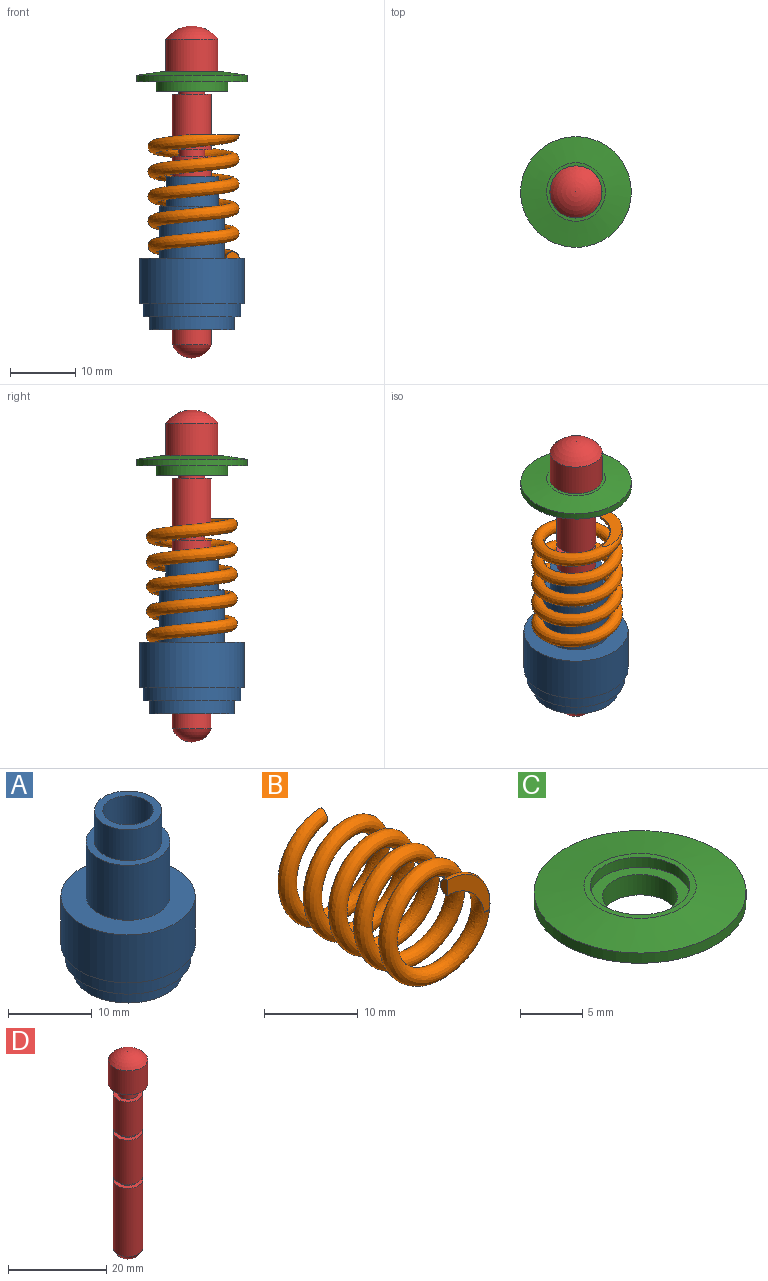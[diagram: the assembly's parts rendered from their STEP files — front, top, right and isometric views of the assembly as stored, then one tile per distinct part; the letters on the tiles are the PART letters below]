
ASSEMBLY  parts=4 mates=4
PART A: 12 faces, bbox 16x16x23.5 mm
  f0: plane 8x8mm, normal (0,0,1), area 22mm2, adj f1,f11
  f1: cylinder r=3mm len=23.5mm, axis (0,0,1), area 443mm2, adj f0,f2
  f2: plane 13x13mm, normal (0,0,-1), area 104.5mm2, adj f1,f3
  f3: cylinder r=6.5mm len=13mm, axis (0,0,1), area 81.7mm2, adj f2,f4
  f4: plane 15x15mm, normal (0,0,-1), area 44mm2, adj f3,f5
  f5: cylinder r=7.5mm len=15mm, axis (0,0,1), area 94.2mm2, adj f4,f6
  f6: plane 16x16mm, normal (0,0,-1), area 24.3mm2, adj f5,f7
  f7: cylinder r=8mm len=16mm, axis (0,0,1), area 351.9mm2, adj f6,f8
  f8: plane 16x16mm, normal (0,0,1), area 122.5mm2, adj f7,f9
  f9: cylinder r=5mm len=10mm, axis (0,0,1), area 251.3mm2, adj f8,f10
  f10: plane 10x10mm, normal (0,0,1), area 28.3mm2, adj f9,f11
  f11: cylinder r=4mm len=8mm, axis (0,0,1), area 113.1mm2, adj f0,f10
PART B: 6 faces, bbox 14.5x21.5x14.5 mm
  f0: bspline ~21x13.99mm, area 1149.5mm2, adj f1,f2,f3,f4,f5
  f1: plane 2.28x1.28mm, normal (1,0,0), area 1.6mm2, adj f0,f3
  f2: plane 2.28x1.28mm, normal (-1,0,0), area 1.6mm2, adj f0,f5
  f3: plane 7.47x6.45mm, normal (0,1,0), area 15.6mm2, adj f0,f1
  f4: plane 0.64x0.07mm, normal (0,0,1), area 0mm2, adj f0,f5
  f5: plane 7.5x6.95mm, normal (0,-1,0), area 15.4mm2, adj f0,f2,f4
PART C: 9 faces, bbox 17x17x3 mm
  f0: cylinder r=3mm len=6mm, axis (0,0,1), area 37.7mm2, adj f1,f8
  f1: plane 11x11mm, normal (0,0,-1), area 66.8mm2, adj f0,f2
  f2: cylinder r=5.5mm len=11mm, axis (0,0,1), area 49mm2, adj f1,f3
  f3: plane 17x17mm, normal (0,0,-1), area 131.9mm2, adj f2,f4
  f4: cylinder r=8.5mm len=17mm, axis (0,0,1), area 53.4mm2, adj f3,f5
  f5: cone r=8.5mm half-angle=81.7deg, axis (0,0,-1), area 165.1mm2, adj f4,f6
  f6: plane 9x9mm, normal (0,0,1), area 13.4mm2, adj f5,f7
  f7: cylinder r=4mm len=8mm, axis (0,0,1), area 25.1mm2, adj f6,f8
  f8: plane 8x8mm, normal (0,0,1), area 22mm2, adj f0,f7
PART D: 15 faces, bbox 8x8x51 mm
  f0: plane 8x8mm, normal (0,0,-1), area 37.7mm2, adj f1,f14
  f1: cylinder r=4mm len=8mm, axis (0,0,-1), area 150.8mm2, adj f0,f2
  f2: sphere r=5mm, area 62.8mm2, adj f1
  f3: sphere r=3.25mm, area 40.8mm2, adj f4
  f4: cylinder r=3mm len=17mm, axis (0,0,-1), area 320.4mm2, adj f3,f5
  f5: plane 6x6mm, normal (0,0,1), area 15.7mm2, adj f4,f6
  f6: cylinder r=2mm len=4mm, axis (0,0,-1), area 12.6mm2, adj f5,f7
  f7: plane 6x6mm, normal (0,0,-1), area 15.7mm2, adj f6,f8
  f8: cylinder r=3mm len=11mm, axis (0,0,-1), area 207.3mm2, adj f7,f9
  f9: plane 6x6mm, normal (0,0,1), area 15.7mm2, adj f8,f10
  f10: cylinder r=2mm len=4mm, axis (0,0,-1), area 12.6mm2, adj f9,f11
  f11: plane 6x6mm, normal (0,0,-1), area 15.7mm2, adj f10,f12
  f12: cylinder r=3mm len=8.5mm, axis (0,0,-1), area 160.2mm2, adj f11,f13
  f13: plane 6x6mm, normal (0,0,1), area 15.7mm2, adj f12,f14
  f14: cylinder r=2mm len=4mm, axis (0,0,-1), area 31.4mm2, adj f0,f13
PLACE A t=(-7.38,-5.02,0.74)mm fixed
PLACE B rot(axis=(0.58,0.58,0.58),120deg) t=(-7.13,-5.01,17.11)mm
PLACE C rot(axis=(0,0,1),106.4deg) t=(-6.26,-8.8,21.59)mm
PLACE D rot(axis=(0,0,-1),90deg) t=(-7.38,-5.02,16.91)mm
MATE fastened B.f5 <-> A.f8  axis (0,0,-1) through (-2.88,-1.52,-1.89)mm
MATE slider D.f1 <-> A.f1  axis (0,0,-1) through (-7.38,-5.02,8.29)mm
MATE planar C.f0 <-> D.f1  axis (0,0,1) through (-7.38,-5.02,25.79)mm
MATE cylindrical C.f0 <-> D.f1  axis (0,0,1) through (-7.38,-5.02,24.79)mm
